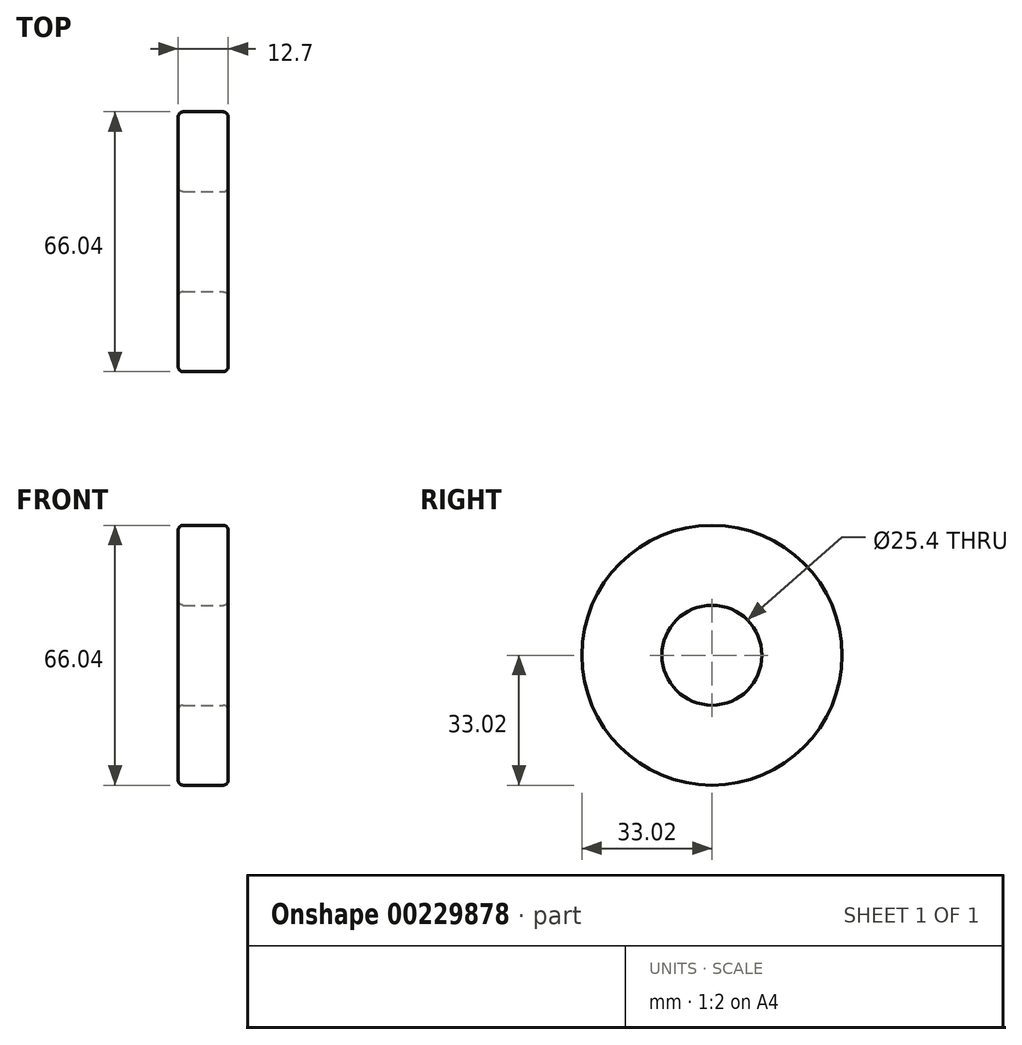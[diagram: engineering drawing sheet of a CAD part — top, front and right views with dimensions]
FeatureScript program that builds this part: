
annotation { "Feature Type Name" : "Feature", "Feature Type Description" : "" }
export const myFeature = defineFeature(function(context is Context, id is Id, definition is map)
    precondition{}
    {
        {
            var Q0;
            Q0=qCreatedBy(makeId("Front.planeOp"),FACE);
            var sketch = newSketch(context, id + "F0", { "sketchPlane" : qUnion([Q0])});
            skLineSegment(sketch, "E0", {"start": v(0, 0) * mm, "end": v(-35.44, 0) * mm});
            skLineSegment(sketch, "E1.bottom", {"start": v(-5.08, 33.02) * mm, "end": v(5.08, 33.02) * mm});
            skLineSegment(sketch, "E1.top", {"start": v(-5.08, 12.7) * mm, "end": v(5.08, 12.7) * mm});
            skLineSegment(sketch, "E1.left", {"start": v(-6.35, 31.75) * mm, "end": v(-6.35, 13.97) * mm});
            skLineSegment(sketch, "E1.right", {"start": v(6.35, 31.75) * mm, "end": v(6.35, 13.97) * mm});
            skPoint(sketch, "E2", {"position": v(0, 33.02) * mm});
            skPoint(sketch, "E3.visualSharp", {"position": v(-6.35, 12.7) * mm});
            skArc(sketch, "E3.filletArc", {"start": v(-6.35, 13.97) * mm, "mid": v(-5.98, 13.07) * mm, "end": v(-5.08, 12.7) * mm});
            skPoint(sketch, "E4.visualSharp", {"position": v(-6.35, 33.02) * mm});
            skArc(sketch, "E4.filletArc", {"start": v(-5.08, 33.02) * mm, "mid": v(-5.98, 32.65) * mm, "end": v(-6.35, 31.75) * mm});
            skPoint(sketch, "E5.visualSharp", {"position": v(6.35, 33.02) * mm});
            skArc(sketch, "E5.filletArc", {"start": v(6.35, 31.75) * mm, "mid": v(5.98, 32.65) * mm, "end": v(5.08, 33.02) * mm});
            skPoint(sketch, "E6.visualSharp", {"position": v(6.35, 12.7) * mm});
            skArc(sketch, "E6.filletArc", {"start": v(5.08, 12.7) * mm, "mid": v(5.98, 13.07) * mm, "end": v(6.35, 13.97) * mm});
            skSolve(sketch);
        }
        {
            var Q0;
            Q0 = qSketchRegion(id + "F0", true);
            var Q1;
            Q1=sQuery(id+"F0.wireOp",EDGE,"E0");
            revolve(context, id + "F1", {"entities" : qUnion([Q0]), "axis" : qUnion([Q1]), "revolveType" : RevolveType.FULL});
        }
    });
